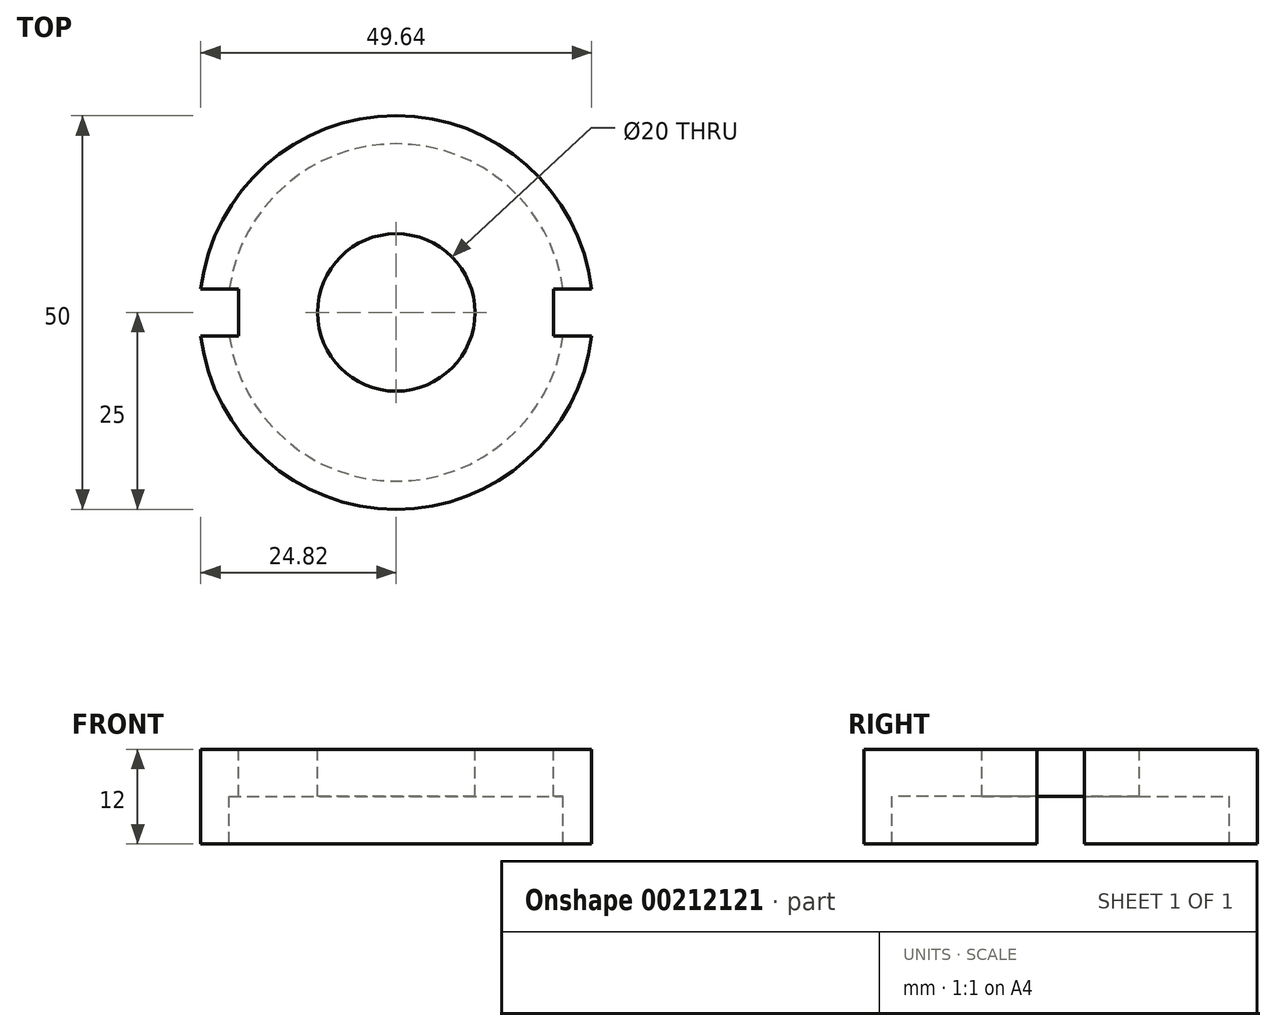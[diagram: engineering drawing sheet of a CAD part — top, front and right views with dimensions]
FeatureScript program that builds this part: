
annotation { "Feature Type Name" : "Feature", "Feature Type Description" : "" }
export const myFeature = defineFeature(function(context is Context, id is Id, definition is map)
    precondition{}
    {
        {
            var Q0;
            Q0=qCreatedBy(makeId("Top.planeOp"),FACE);
            var sketch = newSketch(context, id + "F0", { "sketchPlane" : qUnion([Q0])});
            skCircle(sketch, "E0", {"center": v(0, 0) * mm, "radius": 10 * mm});
            skCircle(sketch, "E1", {"center": v(0, 0) * mm, "radius": 21.42 * mm});
            skCircle(sketch, "E2", {"center": v(0, 0) * mm, "radius": 25 * mm});
            skCircle(sketch, "E3", {"center": v(0, 0) * mm, "radius": 15 * mm});
            skSolve(sketch);
        }
        {
            var Q0;
            Q0=makeQuery(id+"F0.imprint","IMPRINT",FACE,{"disambiguationData":[TD([[makeQuery(id+"F0.imprint","IMPRINT",EDGE,{"derivedFrom":sQuery(id+"F0.wireOp",EDGE,"E1")}),1.0]])]});
            var Q1;
            Q1=makeQuery(id+"F0.imprint","IMPRINT",FACE,{"disambiguationData":[TD([[makeQuery(id+"F0.imprint","IMPRINT",EDGE,{"derivedFrom":sQuery(id+"F0.wireOp",EDGE,"E0")}),-1.0]])]});
            extrude(context, id + "F1", {"entities" : qUnion([Q0, Q1]), "oppositeDirection" : true, "depth" : 6 * mm});
        }
        {
            var Q0;
            Q0=makeQuery(id+"F0.imprint","IMPRINT",FACE,{"disambiguationData":[TD([[makeQuery(id+"F0.imprint","IMPRINT",EDGE,{"derivedFrom":sQuery(id+"F0.wireOp",EDGE,"E1")}),-1.0]])]});
            extrude(context, id + "F2", {"entities" : qUnion([Q0]), "operationType" : NewBodyOperationType.ADD, "oppositeDirection" : true, "depth" : 12 * mm});
        }
        {
            var Q0;
            Q0=qCreatedBy(makeId("Front.planeOp"),FACE);
            var sketch = newSketch(context, id + "F3", { "sketchPlane" : qUnion([Q0])});
            skPoint(sketch, "E4", {"position": v(0, 4) * mm});
            skLineSegment(sketch, "E5.bottom", {"start": v(-15, 8) * mm, "end": v(15, 8) * mm});
            skLineSegment(sketch, "E5.top", {"start": v(-15, 0) * mm, "end": v(15, 0) * mm});
            skLineSegment(sketch, "E5.left", {"start": v(-15, 8) * mm, "end": v(-15, 0) * mm});
            skLineSegment(sketch, "E5.right", {"start": v(15, 8) * mm, "end": v(15, 0) * mm});
            skLineSegment(sketch, "E6.MirrorCS", {"start": v(-15, -8) * mm, "end": v(-15, 0) * mm});
            skLineSegment(sketch, "E7.MirrorCS", {"start": v(-15, -8) * mm, "end": v(15, -8) * mm});
            skLineSegment(sketch, "E8.MirrorCS", {"start": v(15, -8) * mm, "end": v(15, 0) * mm});
            skSolve(sketch);
        }
        {
            var Q0;
            Q0=qCreatedBy(makeId("Top.planeOp"),FACE);
            var sketch = newSketch(context, id + "F4", { "sketchPlane" : qUnion([Q0])});
            skLineSegment(sketch, "E9", {"start": v(0, 0) * mm, "end": v(25, 0) * mm, "construction": true});
            skLineSegment(sketch, "E10.bottom", {"start": v(30, -3) * mm, "end": v(20, -3) * mm});
            skLineSegment(sketch, "E10.top", {"start": v(30, 3) * mm, "end": v(20, 3) * mm});
            skLineSegment(sketch, "E10.left", {"start": v(30, -3) * mm, "end": v(30, 3) * mm});
            skLineSegment(sketch, "E10.right", {"start": v(20, -3) * mm, "end": v(20, 3) * mm});
            skPoint(sketch, "E10.middle", {"position": v(25, 0) * mm});
            skLineSegment(sketch, "E11.1.0", {"start": v(-30, 3) * mm, "end": v(-20, 3) * mm});
            skLineSegment(sketch, "E11.1.1", {"start": v(-30, 3) * mm, "end": v(-30, -3) * mm});
            skLineSegment(sketch, "E11.1.2", {"start": v(-30, -3) * mm, "end": v(-20, -3) * mm});
            skLineSegment(sketch, "E11.1.3", {"start": v(-20, 3) * mm, "end": v(-20, -3) * mm});
            skPoint(sketch, "E11.center", {"position": v(0, 0) * mm});
            skSolve(sketch);
        }
        {
            var Q0;
            Q0=makeQuery(id+"F4.imprint","IMPRINT",FACE,{"disambiguationData":[TD([[makeQuery(id+"F4.imprint","IMPRINT",EDGE,{"derivedFrom":sQuery(id+"F4.wireOp",EDGE,"E10.bottom")}),-1.0]])]});
            var Q1;
            Q1=makeQuery(id+"F4.imprint","IMPRINT",FACE,{"disambiguationData":[TD([[makeQuery(id+"F4.imprint","IMPRINT",EDGE,{"derivedFrom":sQuery(id+"F4.wireOp",EDGE,"E11.1.0")}),-1.0]])]});
            extrude(context, id + "F5", {"entities" : qUnion([Q0, Q1]), "operationType" : NewBodyOperationType.REMOVE, "oppositeDirection" : true, "depth" : 25 * mm});
        }
    });
